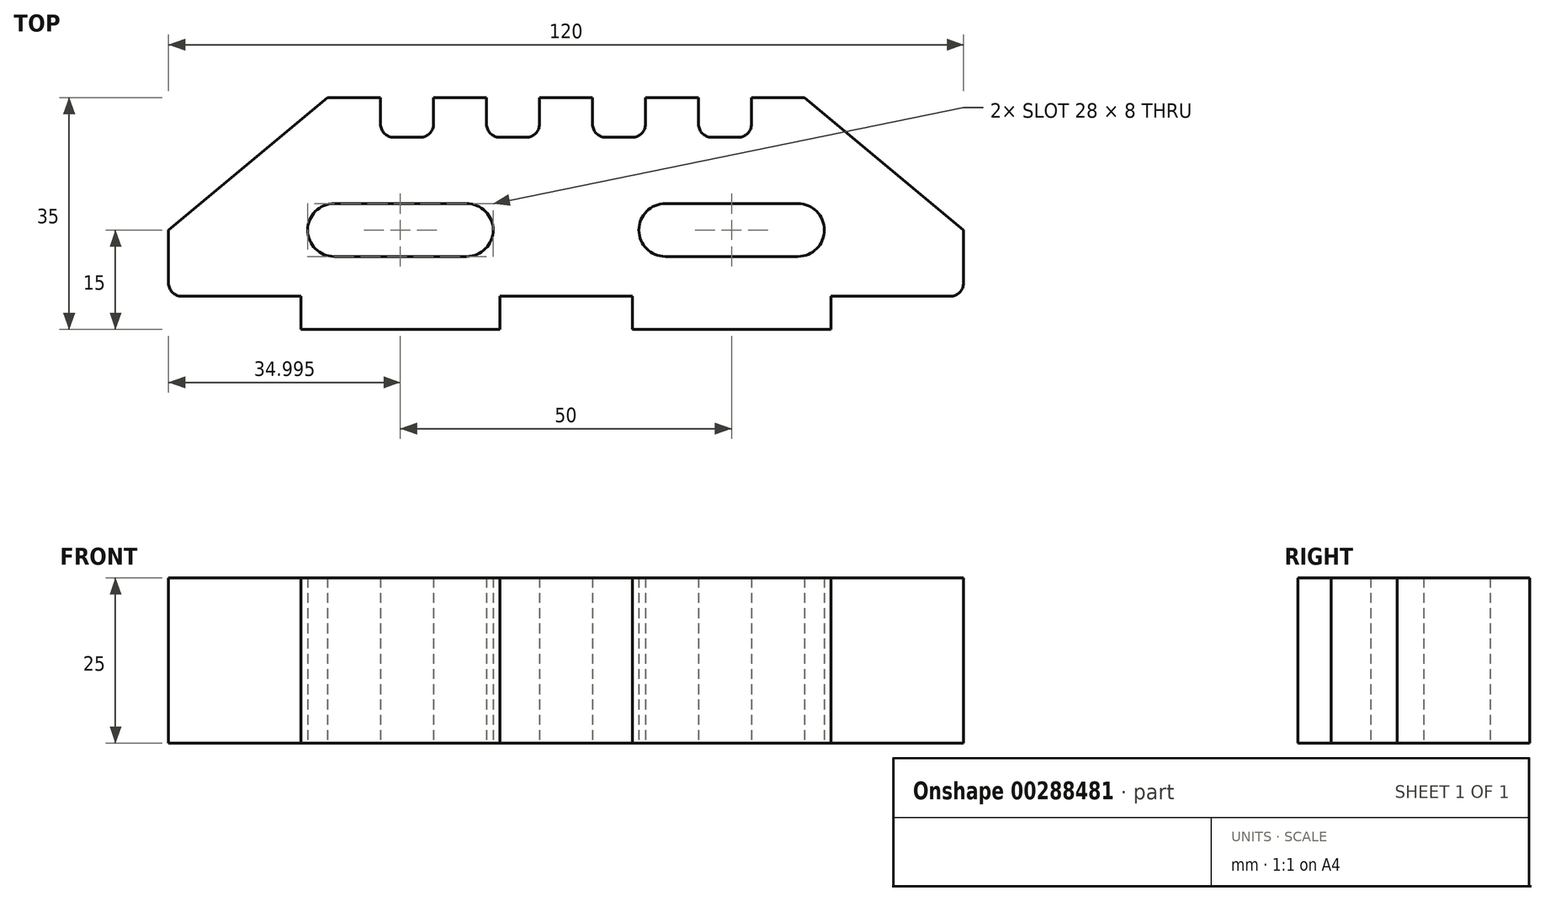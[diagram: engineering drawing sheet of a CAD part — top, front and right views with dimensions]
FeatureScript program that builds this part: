
annotation { "Feature Type Name" : "Feature", "Feature Type Description" : "" }
export const myFeature = defineFeature(function(context is Context, id is Id, definition is map)
    precondition{}
    {
        {
            var Q0;
            Q0=qCreatedBy(makeId("Top.planeOp"),FACE);
            var sketch = newSketch(context, id + "F0", { "sketchPlane" : qUnion([Q0])});
            skLineSegment(sketch, "E0", {"start": v(-34.81, -10) * mm, "end": v(-16.81, -10) * mm});
            skLineSegment(sketch, "E1", {"start": v(-16.81, -10) * mm, "end": v(-16.81, -15) * mm});
            skLineSegment(sketch, "E2", {"start": v(-16.81, -15) * mm, "end": v(13.19, -15) * mm});
            skLineSegment(sketch, "E3", {"start": v(13.19, -15) * mm, "end": v(13.19, -10) * mm});
            skLineSegment(sketch, "E4", {"start": v(13.19, -10) * mm, "end": v(33.19, -10) * mm});
            skLineSegment(sketch, "E5", {"start": v(33.19, -10) * mm, "end": v(33.19, -15) * mm});
            skLineSegment(sketch, "E6", {"start": v(33.19, -15) * mm, "end": v(63.19, -15) * mm});
            skLineSegment(sketch, "E7", {"start": v(-36.81, -8) * mm, "end": v(-36.81, 0) * mm});
            skLineSegment(sketch, "E8", {"start": v(-36.81, 0) * mm, "end": v(-12.81, 20) * mm});
            skLineSegment(sketch, "E9", {"start": v(-12.81, 20) * mm, "end": v(-4.81, 20) * mm});
            skLineSegment(sketch, "E10", {"start": v(-4.81, 20) * mm, "end": v(-4.81, 16) * mm});
            skLineSegment(sketch, "E11", {"start": v(-2.81, 14) * mm, "end": v(1.19, 14) * mm});
            skLineSegment(sketch, "E12", {"start": v(3.19, 16) * mm, "end": v(3.19, 20) * mm});
            skLineSegment(sketch, "E13", {"start": v(3.19, 20) * mm, "end": v(11.19, 20) * mm});
            skLineSegment(sketch, "E14", {"start": v(11.19, 20) * mm, "end": v(11.19, 16) * mm});
            skLineSegment(sketch, "E15", {"start": v(13.19, 14) * mm, "end": v(17.19, 14) * mm});
            skLineSegment(sketch, "E16", {"start": v(19.19, 16) * mm, "end": v(19.19, 20) * mm});
            skLineSegment(sketch, "E17", {"start": v(19.19, 20) * mm, "end": v(27.19, 20) * mm});
            skLineSegment(sketch, "E18", {"start": v(27.19, 20) * mm, "end": v(27.19, 16) * mm});
            skLineSegment(sketch, "E19", {"start": v(29.19, 14) * mm, "end": v(33.19, 14) * mm});
            skLineSegment(sketch, "E20", {"start": v(35.19, 16) * mm, "end": v(35.19, 20) * mm});
            skLineSegment(sketch, "E21", {"start": v(35.19, 20) * mm, "end": v(43.19, 20) * mm});
            skLineSegment(sketch, "E22", {"start": v(43.19, 20) * mm, "end": v(43.19, 16) * mm});
            skLineSegment(sketch, "E23", {"start": v(45.19, 14) * mm, "end": v(49.19, 14) * mm});
            skLineSegment(sketch, "E24", {"start": v(51.19, 16) * mm, "end": v(51.19, 20) * mm});
            skLineSegment(sketch, "E25", {"start": v(63.19, -15) * mm, "end": v(63.19, -10) * mm});
            skLineSegment(sketch, "E26", {"start": v(63.19, -10) * mm, "end": v(81.19, -10) * mm});
            skLineSegment(sketch, "E27", {"start": v(51.19, 20) * mm, "end": v(59.19, 20) * mm});
            skLineSegment(sketch, "E28", {"start": v(59.19, 20) * mm, "end": v(83.19, 0) * mm});
            skLineSegment(sketch, "E29", {"start": v(83.19, 0) * mm, "end": v(83.19, -8) * mm});
            skPoint(sketch, "E30.visualSharp", {"position": v(-4.81, 14) * mm});
            skArc(sketch, "E30.filletArc", {"start": v(-4.81, 16) * mm, "mid": v(-4.23, 14.59) * mm, "end": v(-2.81, 14) * mm});
            skPoint(sketch, "E31.visualSharp", {"position": v(3.19, 14) * mm});
            skArc(sketch, "E31.filletArc", {"start": v(1.19, 14) * mm, "mid": v(2.6, 14.59) * mm, "end": v(3.19, 16) * mm});
            skPoint(sketch, "E32.visualSharp", {"position": v(11.19, 14) * mm});
            skArc(sketch, "E32.filletArc", {"start": v(11.19, 16) * mm, "mid": v(11.77, 14.59) * mm, "end": v(13.19, 14) * mm});
            skPoint(sketch, "E33.visualSharp", {"position": v(19.19, 14) * mm});
            skArc(sketch, "E33.filletArc", {"start": v(17.19, 14) * mm, "mid": v(18.6, 14.59) * mm, "end": v(19.19, 16) * mm});
            skPoint(sketch, "E34.visualSharp", {"position": v(27.19, 14) * mm});
            skArc(sketch, "E34.filletArc", {"start": v(27.19, 16) * mm, "mid": v(27.77, 14.59) * mm, "end": v(29.19, 14) * mm});
            skPoint(sketch, "E35.visualSharp", {"position": v(35.19, 14) * mm});
            skArc(sketch, "E35.filletArc", {"start": v(33.19, 14) * mm, "mid": v(34.6, 14.59) * mm, "end": v(35.19, 16) * mm});
            skPoint(sketch, "E36.visualSharp", {"position": v(43.19, 14) * mm});
            skArc(sketch, "E36.filletArc", {"start": v(43.19, 16) * mm, "mid": v(43.77, 14.59) * mm, "end": v(45.19, 14) * mm});
            skPoint(sketch, "E37.visualSharp", {"position": v(51.19, 14) * mm});
            skArc(sketch, "E37.filletArc", {"start": v(49.19, 14) * mm, "mid": v(50.6, 14.59) * mm, "end": v(51.19, 16) * mm});
            skPoint(sketch, "E38.visualSharp", {"position": v(-36.81, -10) * mm});
            skArc(sketch, "E38.filletArc", {"start": v(-36.81, -8) * mm, "mid": v(-36.23, -9.41) * mm, "end": v(-34.81, -10) * mm});
            skPoint(sketch, "E39.visualSharp", {"position": v(83.19, -10) * mm});
            skArc(sketch, "E39.filletArc", {"start": v(81.19, -10) * mm, "mid": v(82.6, -9.41) * mm, "end": v(83.19, -8) * mm});
            skPoint(sketch, "E40.startSnap0", {"position": v(23.19, 20) * mm});
            skLineSegment(sketch, "E41", {"start": v(58.19, -4) * mm, "end": v(38.19, -4) * mm});
            skLineSegment(sketch, "E42", {"start": v(38.19, 4) * mm, "end": v(58.19, 4) * mm});
            skArc(sketch, "E43", {"start": v(38.19, 4) * mm, "mid": v(34.19, 0) * mm, "end": v(38.19, -4) * mm});
            skArc(sketch, "E44", {"start": v(58.19, -4) * mm, "mid": v(62.19, 0) * mm, "end": v(58.19, 4) * mm});
            skLineSegment(sketch, "E45", {"start": v(8.19, -4) * mm, "end": v(-11.81, -4) * mm});
            skLineSegment(sketch, "E46", {"start": v(8.19, 4) * mm, "end": v(-11.81, 4) * mm});
            skArc(sketch, "E47", {"start": v(8.19, -4) * mm, "mid": v(12.19, 0) * mm, "end": v(8.19, 4) * mm});
            skArc(sketch, "E48", {"start": v(-11.81, 4) * mm, "mid": v(-15.81, 0) * mm, "end": v(-11.81, -4) * mm});
            skSolve(sketch);
        }
        {
            var Q0;
            Q0 = qSketchRegion(id + "F0", true);
            var Q1;
            Q1=makeQuery(id+"F0.imprint","IMPRINT",FACE,{"disambiguationData":[TD([[makeQuery(id+"F0.imprint","IMPRINT",EDGE,{"derivedFrom":sQuery(id+"F0.wireOp",EDGE,"E0")}),1.0]])]});
            extrude(context, id + "F1", {"entities" : qUnion([Q0, Q1]), "depth" : 25 * mm});
        }
    });
